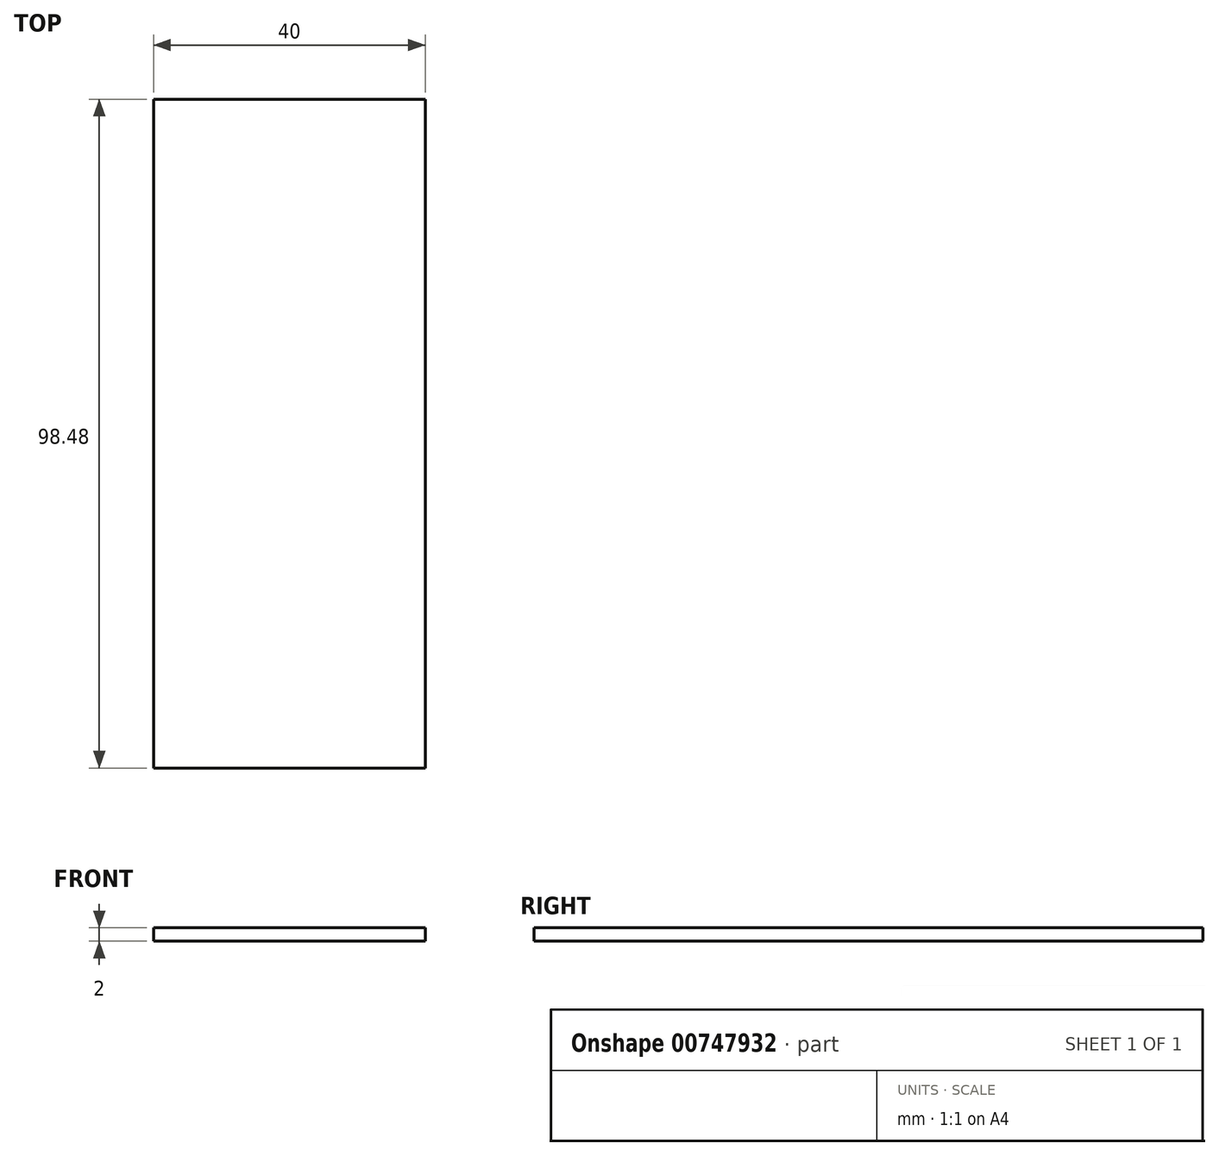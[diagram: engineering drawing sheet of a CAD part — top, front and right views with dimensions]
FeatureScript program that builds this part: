
annotation { "Feature Type Name" : "Feature", "Feature Type Description" : "" }
export const myFeature = defineFeature(function(context is Context, id is Id, definition is map)
    precondition{}
    {
        {
            var Q0;
            Q0=qCreatedBy(makeId("Top.planeOp"),FACE);
            var sketch = newSketch(context, id + "F0", { "sketchPlane" : qUnion([Q0])});
            skLineSegment(sketch, "E0", {"start": v(0, 0) * mm, "end": v(0, 34.17) * mm});
            skLineSegment(sketch, "E1", {"start": v(0, 34.17) * mm, "end": v(0, -31) * mm, "construction": true});
            skLineSegment(sketch, "E2", {"start": v(0, 34.17) * mm, "end": v(-20, 34.17) * mm, "construction": true});
            skLineSegment(sketch, "E3.bottom", {"start": v(-20, 34.17) * mm, "end": v(20, 34.17) * mm});
            skLineSegment(sketch, "E3.top", {"start": v(-20, -31) * mm, "end": v(20, -31) * mm});
            skLineSegment(sketch, "E3.left", {"start": v(-20, 34.17) * mm, "end": v(-20, -31) * mm});
            skLineSegment(sketch, "E3.right", {"start": v(20, 34.17) * mm, "end": v(20, -31) * mm});
            skLineSegment(sketch, "E4.top", {"start": v(-20, 67.48) * mm, "end": v(20, 67.48) * mm});
            skLineSegment(sketch, "E4.left", {"start": v(-20, 34.17) * mm, "end": v(-20, 67.48) * mm});
            skLineSegment(sketch, "E4.right", {"start": v(20, 34.17) * mm, "end": v(20, 67.48) * mm});
            skSolve(sketch);
        }
        {
            var Q0;
            Q0 = qSketchRegion(id + "F0", true);
            extrude(context, id + "F1", {"entities" : qUnion([Q0]), "depth" : 2 * mm, "offsetDistance" : 25 * mm});
        }
    });
